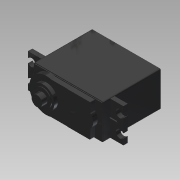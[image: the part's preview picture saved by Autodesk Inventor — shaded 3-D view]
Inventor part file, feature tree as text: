
AUTODESK INVENTOR PART (.ipt)
format: ipt  version: 2015 SP1 (Build 190203100, 203)  size: 407,552 bytes
history: native  units: in
note: dims shown in document units (in); Inventor stores cm internally (conversion verified against a paired STEP export)
features: projected_geometry x7, other x3, sketch x3, imported_body x2
ambient origin geometry x8: Origin, YZ Plane, XZ Plane, XY Plane, X Axis, Y Axis, Z Axis, Center Point
bodies: Body1 (feature_tree), Body2 (feature_tree)
feature tree (15):
  other  "Boss-Extrude1"
  other  "servo1"
  sketch  "Sketch2"  dims[d4=0.0875in]
  sketch  "Sketch4"  dims[d5=0.386in]
  sketch  "Sketch5"  dims[d6=1.937in d7=0.775in d8=0.6725in]
  other  "Boss-Extrude3"
  imported_body  "Base1"
  imported_body  "Base2"
  projected_geometry  "Projected Loop2"
  projected_geometry  "Projected Loop3"
  projected_geometry  "Projected Loop4"
  projected_geometry  "Projected Loop5"
  projected_geometry  "Projected Loop6"
  projected_geometry  "Projected Loop7"
  projected_geometry  "Projected Loop8"
